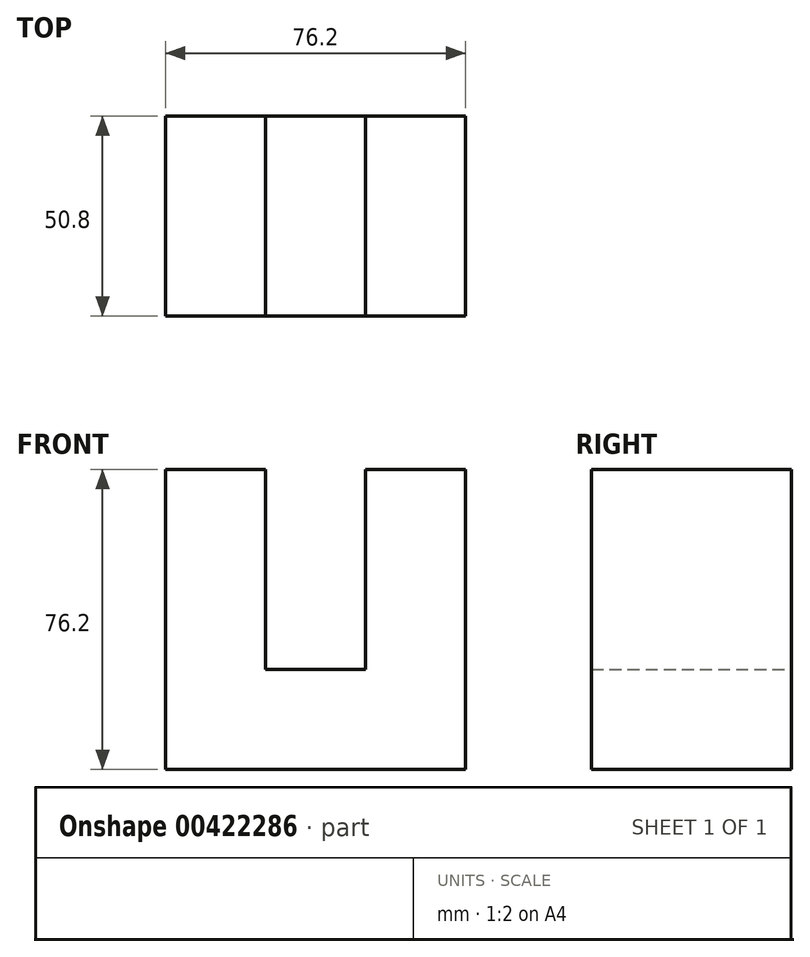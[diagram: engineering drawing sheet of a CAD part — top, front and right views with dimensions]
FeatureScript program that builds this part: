
annotation { "Feature Type Name" : "Feature", "Feature Type Description" : "" }
export const myFeature = defineFeature(function(context is Context, id is Id, definition is map)
    precondition{}
    {
        {
            var Q0;
            Q0=qCreatedBy(makeId("Front.planeOp"),FACE);
            var sketch = newSketch(context, id + "F0", { "sketchPlane" : qUnion([Q0])});
            skLineSegment(sketch, "E0", {"start": v(-60.78, 39.01) * mm, "end": v(-60.78, -37.19) * mm});
            skLineSegment(sketch, "E1", {"start": v(-60.78, -37.19) * mm, "end": v(15.42, -37.19) * mm});
            skLineSegment(sketch, "E2", {"start": v(15.42, -37.19) * mm, "end": v(15.42, 39.01) * mm});
            skLineSegment(sketch, "E3", {"start": v(15.42, 39.01) * mm, "end": v(-9.98, 39.01) * mm});
            skLineSegment(sketch, "E4", {"start": v(-60.78, 39.01) * mm, "end": v(-35.38, 39.01) * mm});
            skLineSegment(sketch, "E5", {"start": v(-35.38, 39.01) * mm, "end": v(-35.38, -11.79) * mm});
            skLineSegment(sketch, "E6", {"start": v(-9.98, 39.01) * mm, "end": v(-9.98, -11.79) * mm});
            skLineSegment(sketch, "E7", {"start": v(-35.38, -11.79) * mm, "end": v(-9.98, -11.79) * mm});
            skSolve(sketch);
        }
        {
            var Q0;
            Q0 = qSketchRegion(id + "F0", true);
            extrude(context, id + "F1", {"entities" : qUnion([Q0]), "depth" : 50.8 * mm});
        }
    });
